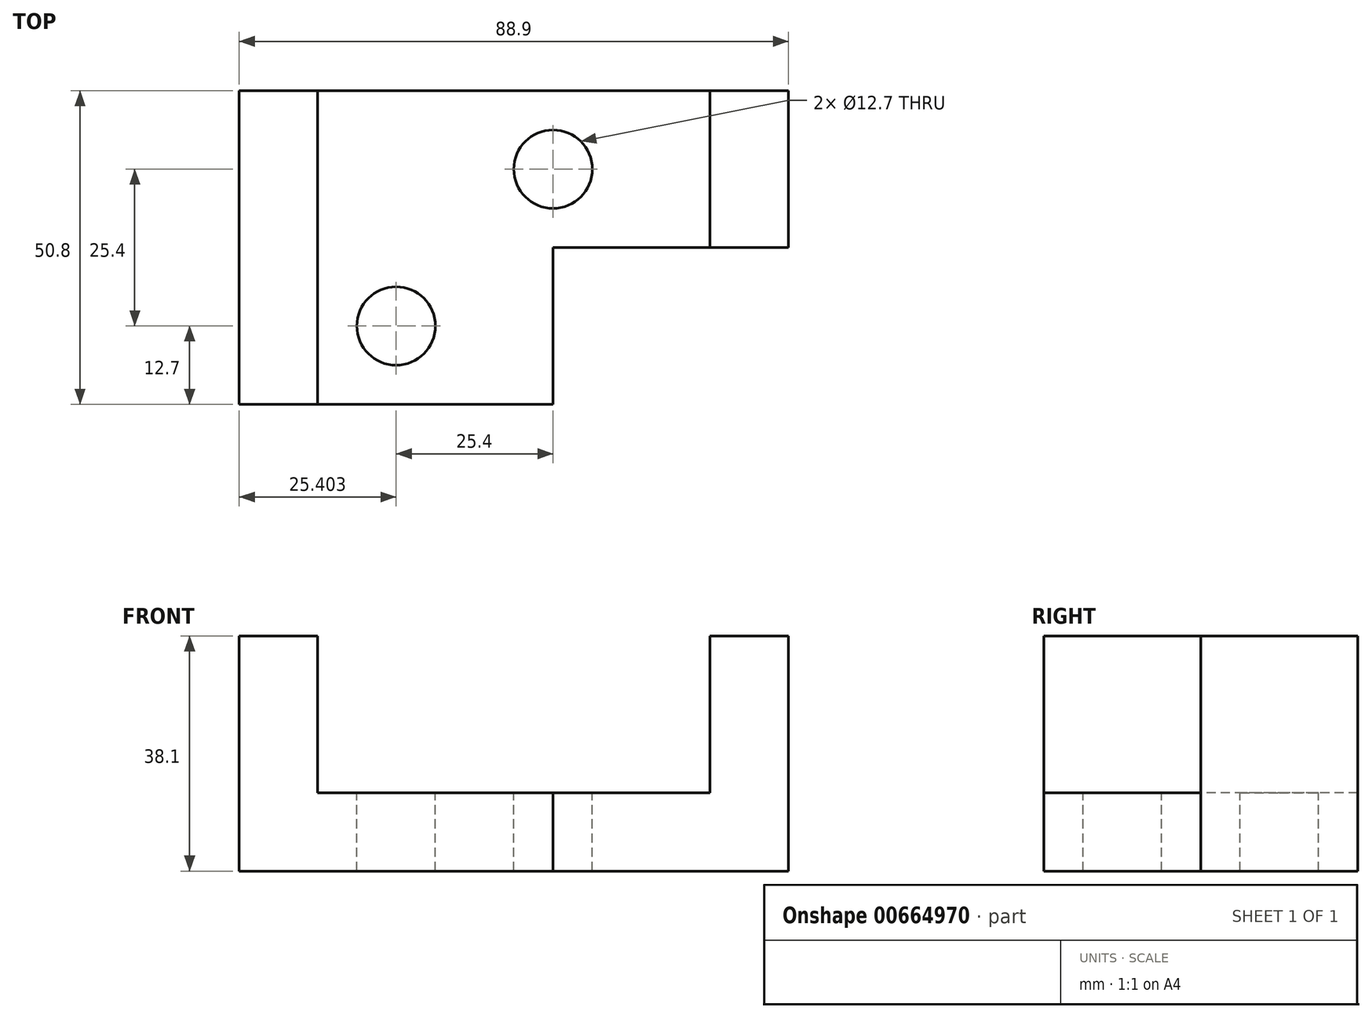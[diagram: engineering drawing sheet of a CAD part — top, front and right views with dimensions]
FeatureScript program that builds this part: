
annotation { "Feature Type Name" : "Feature", "Feature Type Description" : "" }
export const myFeature = defineFeature(function(context is Context, id is Id, definition is map)
    precondition{}
    {
        {
            var Q0;
            Q0=qCreatedBy(makeId("Front.planeOp"),FACE);
            var sketch = newSketch(context, id + "F0", { "sketchPlane" : qUnion([Q0])});
            skLineSegment(sketch, "E0.bottom", {"start": v(-43.4, 13.07) * mm, "end": v(45.5, 13.07) * mm});
            skLineSegment(sketch, "E0.top", {"start": v(-43.4, -25.03) * mm, "end": v(45.5, -25.03) * mm});
            skLineSegment(sketch, "E0.left", {"start": v(-43.4, 13.07) * mm, "end": v(-43.4, -25.03) * mm});
            skLineSegment(sketch, "E0.right", {"start": v(45.5, 13.07) * mm, "end": v(45.5, -25.03) * mm});
            skSolve(sketch);
        }
        {
            var Q0;
            Q0 = qSketchRegion(id + "F0", true);
            extrude(context, id + "F1", {"entities" : qUnion([Q0]), "depth" : 50.8 * mm, "offsetDistance" : 25.4 * mm});
        }
        {
            var Q0;
            Q0=makeQuery(id+"F1.opExtrude","CAP_FACE",FACE,{"disambiguationData":[OSD([sQuery(id+"F0.wireOp",EDGE,"E0.bottom"),sQuery(id+"F0.wireOp",EDGE,"E0.top"),sQuery(id+"F0.wireOp",EDGE,"E0.left"),sQuery(id+"F0.wireOp",EDGE,"E0.right")])],"isStart":false});
            var sketch = newSketch(context, id + "F2", { "sketchPlane" : qUnion([Q0])});
            skLineSegment(sketch, "E1.bottom", {"start": v(-30.7, 13.07) * mm, "end": v(32.8, 13.07) * mm});
            skLineSegment(sketch, "E1.top", {"start": v(-30.7, -12.33) * mm, "end": v(32.8, -12.33) * mm});
            skLineSegment(sketch, "E1.left", {"start": v(-30.7, 13.07) * mm, "end": v(-30.7, -12.33) * mm});
            skLineSegment(sketch, "E1.right", {"start": v(32.8, 13.07) * mm, "end": v(32.8, -12.33) * mm});
            skSolve(sketch);
        }
        {
            var Q0;
            Q0 = qSketchRegion(id + "F2", true);
            extrude(context, id + "F3", {"entities" : qUnion([Q0]), "operationType" : NewBodyOperationType.REMOVE, "oppositeDirection" : true, "depth" : 50.8 * mm, "offsetDistance" : 25.4 * mm});
        }
        {
            var Q0;
            Q0=makeQuery(id+"F1.opExtrude","SWEPT_FACE",FACE,{"disambiguationData":[OSD([sQuery(id+"F0.wireOp",EDGE,"E0.right")])]});
            var sketch = newSketch(context, id + "F4", { "sketchPlane" : qUnion([Q0])});
            skLineSegment(sketch, "E2.bottom", {"start": v(-50.8, 13.07) * mm, "end": v(-25.4, 13.07) * mm});
            skLineSegment(sketch, "E2.top", {"start": v(-50.8, -25.03) * mm, "end": v(-25.4, -25.03) * mm});
            skLineSegment(sketch, "E2.left", {"start": v(-50.8, 13.07) * mm, "end": v(-50.8, -25.03) * mm});
            skLineSegment(sketch, "E2.right", {"start": v(-25.4, 13.07) * mm, "end": v(-25.4, -25.03) * mm});
            skSolve(sketch);
        }
        {
            var Q0;
            Q0 = qSketchRegion(id + "F4", true);
            extrude(context, id + "F5", {"entities" : qUnion([Q0]), "operationType" : NewBodyOperationType.REMOVE, "oppositeDirection" : true, "depth" : 38.1 * mm, "offsetDistance" : 25.4 * mm});
        }
        {
            var Q0;
            Q0=makeQuery(id+"F3.boolean.opBoolean","COPY",FACE,{"derivedFrom":makeQuery(id+"F3.opExtrude","SWEPT_FACE",FACE,{"disambiguationData":[OSD([sQuery(id+"F2.wireOp",EDGE,"E1.top")])]})});
            var sketch = newSketch(context, id + "F6", { "sketchPlane" : qUnion([Q0])});
            skCircle(sketch, "E3", {"center": v(-18, -38.1) * mm, "radius": 6.35 * mm});
            skSolve(sketch);
        }
        {
            var Q0;
            Q0 = qSketchRegion(id + "F6", true);
            extrude(context, id + "F7", {"entities" : qUnion([Q0]), "operationType" : NewBodyOperationType.REMOVE, "oppositeDirection" : true, "depth" : 25.4 * mm, "offsetDistance" : 25.4 * mm});
        }
        {
            var Q0;
            Q0=makeQuery(id+"F3.boolean.opBoolean","COPY",FACE,{"derivedFrom":makeQuery(id+"F3.opExtrude","SWEPT_FACE",FACE,{"disambiguationData":[OSD([sQuery(id+"F2.wireOp",EDGE,"E1.top")])]})});
            var sketch = newSketch(context, id + "F8", { "sketchPlane" : qUnion([Q0])});
            skCircle(sketch, "E4", {"center": v(7.4, -12.7) * mm, "radius": 6.35 * mm});
            skSolve(sketch);
        }
        {
            var Q0;
            Q0 = qSketchRegion(id + "F8", true);
            extrude(context, id + "F9", {"entities" : qUnion([Q0]), "operationType" : NewBodyOperationType.REMOVE, "oppositeDirection" : true, "depth" : 25.4 * mm, "offsetDistance" : 25.4 * mm});
        }
    });
